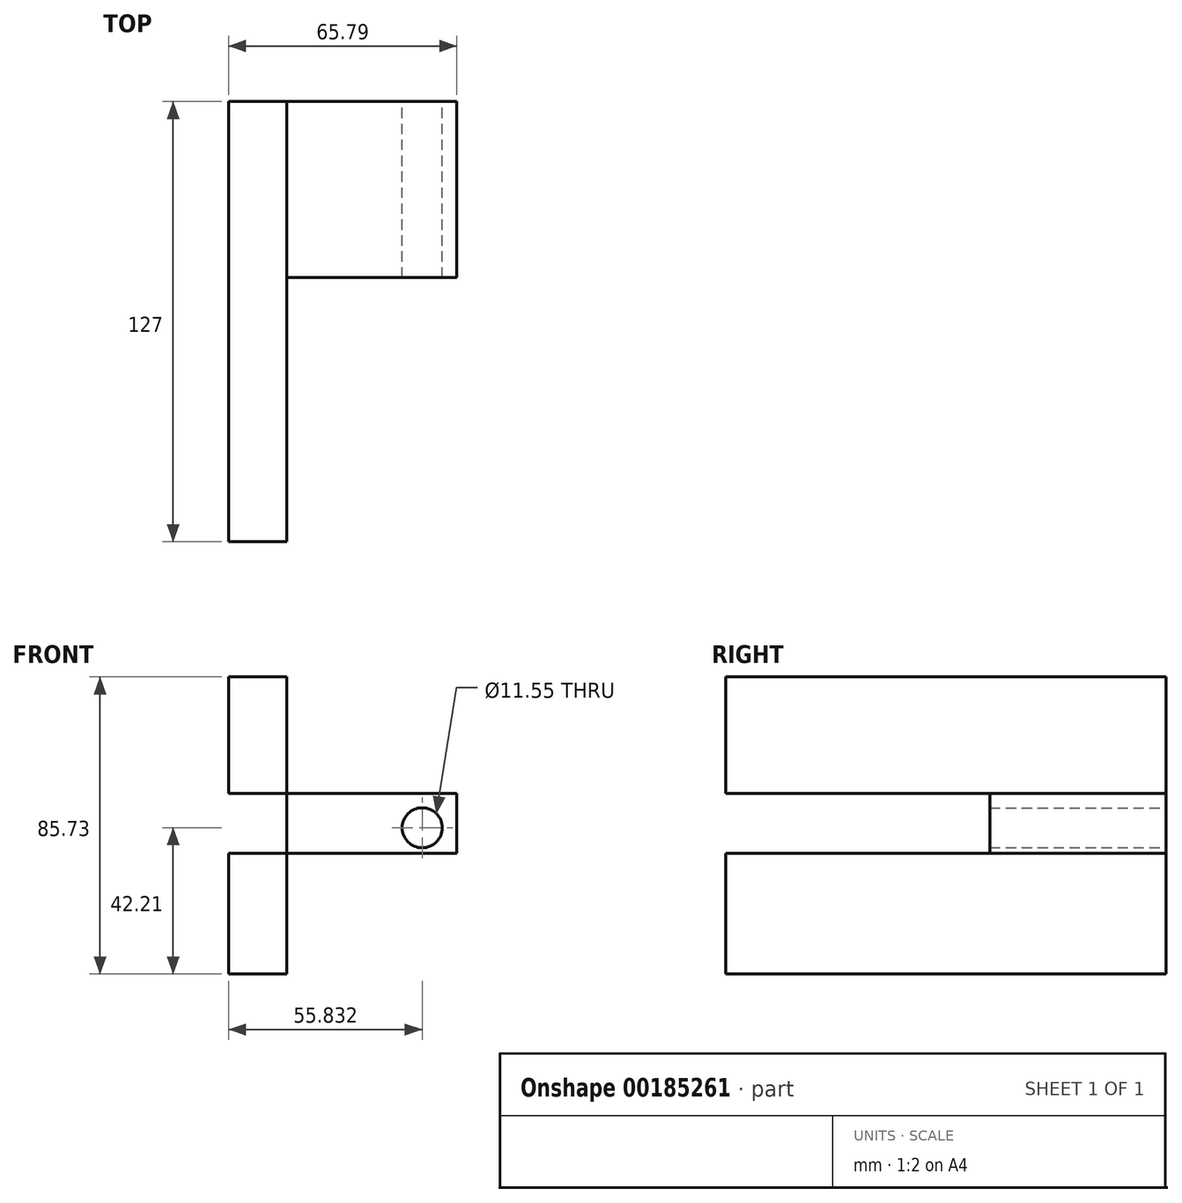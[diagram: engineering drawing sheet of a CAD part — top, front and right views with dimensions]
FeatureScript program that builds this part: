
annotation { "Feature Type Name" : "Feature", "Feature Type Description" : "" }
export const myFeature = defineFeature(function(context is Context, id is Id, definition is map)
    precondition{}
    {
        {
            var Q0;
            Q0=qCreatedBy(makeId("Front.planeOp"),FACE);
            var sketch = newSketch(context, id + "F0", { "sketchPlane" : qUnion([Q0])});
            skLineSegment(sketch, "E0.bottom", {"start": v(-76.28, 43.52) * mm, "end": v(-59.5, 43.52) * mm});
            skLineSegment(sketch, "E0.top", {"start": v(-76.28, -42.2) * mm, "end": v(-59.5, -42.2) * mm});
            skLineSegment(sketch, "E0.left", {"start": v(-76.28, 43.52) * mm, "end": v(-76.28, -42.2) * mm});
            skLineSegment(sketch, "E0.right", {"start": v(-59.5, 43.52) * mm, "end": v(-59.5, -42.2) * mm});
            skLineSegment(sketch, "E1.bottom", {"start": v(-76.28, 9.96) * mm, "end": v(-10.49, 9.96) * mm});
            skLineSegment(sketch, "E1.top", {"start": v(-76.28, -7.34) * mm, "end": v(-10.49, -7.34) * mm});
            skLineSegment(sketch, "E1.left", {"start": v(-76.28, 9.96) * mm, "end": v(-76.28, -7.34) * mm});
            skLineSegment(sketch, "E1.right", {"start": v(-10.49, 9.96) * mm, "end": v(-10.49, -7.34) * mm});
            skCircle(sketch, "E2", {"center": v(-20.45, 0) * mm, "radius": 5.77 * mm});
            skSolve(sketch);
        }
        {
            var Q0;
            {var subQ0=sQuery(id+"F0.wireOp",EDGE,"E0.bottom");Q0=makeQuery(id+"F0.imprint","IMPRINT",FACE,{"disambiguationData":[TD([[makeQuery(id+"F0.imprint","IMPRINT",EDGE,{"derivedFrom":subQ0}),-1.0]])]});}
            var Q1;
            {var subQ5=sQuery(id+"F0.wireOp",EDGE,"E1.left");Q1=makeQuery(id+"F0.imprint","IMPRINT",FACE,{"disambiguationData":[TD([[makeQuery(id+"F0.imprint","IMPRINT",EDGE,{"derivedFrom":subQ5}),1.0]])]});}
            var Q2;
            {var subQ0=sQuery(id+"F0.wireOp",EDGE,"E0.top");Q2=makeQuery(id+"F0.imprint","IMPRINT",FACE,{"disambiguationData":[TD([[makeQuery(id+"F0.imprint","IMPRINT",EDGE,{"derivedFrom":subQ0}),1.0]])]});}
            extrude(context, id + "F1", {"entities" : qUnion([Q0, Q1, Q2]), "depth" : 127 * mm});
        }
        {
            var Q0;
            {var subQ0=sQuery(id+"F0.wireOp",EDGE,"E1.right");Q0=makeQuery(id+"F0.imprint","IMPRINT",FACE,{"disambiguationData":[TD([[makeQuery(id+"F0.imprint","IMPRINT",EDGE,{"derivedFrom":subQ0}),-1.0]])]});}
            extrude(context, id + "F2", {"entities" : qUnion([Q0]), "operationType" : NewBodyOperationType.ADD, "depth" : 50.8 * mm});
        }
    });
